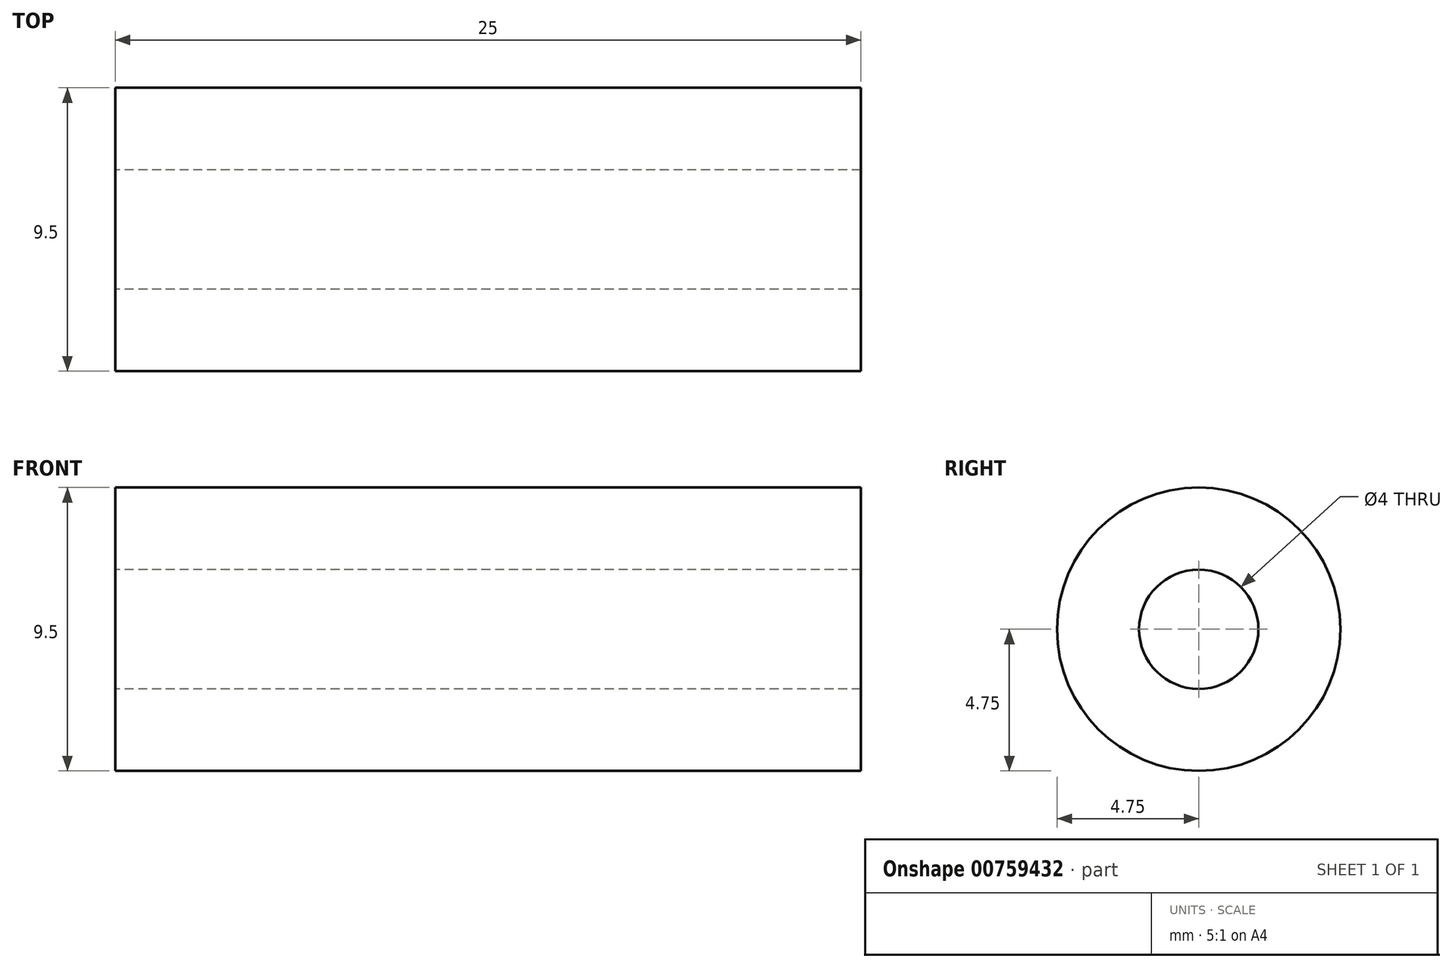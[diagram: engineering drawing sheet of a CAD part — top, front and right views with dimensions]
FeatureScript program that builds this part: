
annotation { "Feature Type Name" : "Feature", "Feature Type Description" : "" }
export const myFeature = defineFeature(function(context is Context, id is Id, definition is map)
    precondition{}
    {
        {
            var Q0;
            Q0=qCreatedBy(makeId("Right.planeOp"),FACE);
            var sketch = newSketch(context, id + "F0", { "sketchPlane" : qUnion([Q0])});
            skCircle(sketch, "E0", {"center": v(0, 0) * mm, "radius": 4.75 * mm});
            skCircle(sketch, "E1", {"center": v(0, 0) * mm, "radius": 2 * mm});
            skSolve(sketch);
        }
        {
            var Q0;
            Q0 = qSketchRegion(id + "F0", true);
            extrude(context, id + "F1", {"entities" : qUnion([Q0]), "endBound" : BoundingType.SYMMETRIC, "depth" : 25 * mm, "offsetDistance" : 25 * mm});
        }
    });
